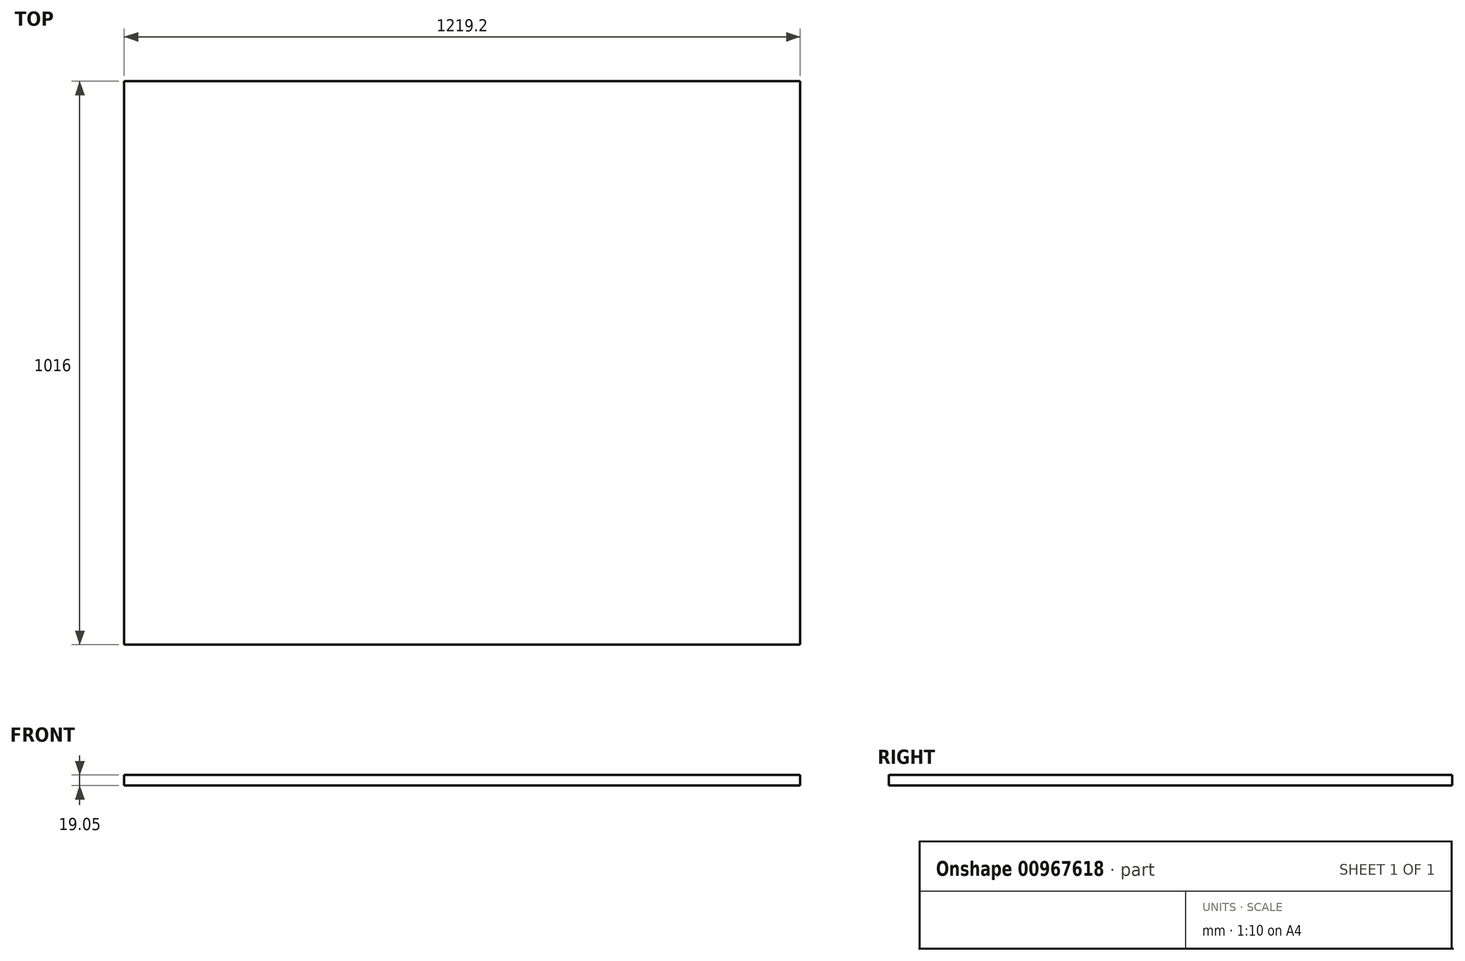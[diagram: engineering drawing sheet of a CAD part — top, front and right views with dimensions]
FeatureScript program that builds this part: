
annotation { "Feature Type Name" : "Feature", "Feature Type Description" : "" }
export const myFeature = defineFeature(function(context is Context, id is Id, definition is map)
    precondition{}
    {
        {
            var Q0;
            Q0=qCreatedBy(makeId("Top.planeOp"),FACE);
            var sketch = newSketch(context, id + "F0", { "sketchPlane" : qUnion([Q0])});
            skLineSegment(sketch, "E0.bottom", {"start": v(609.6, 508) * mm, "end": v(-609.6, 508) * mm});
            skLineSegment(sketch, "E0.top", {"start": v(609.6, -508) * mm, "end": v(-609.6, -508) * mm});
            skLineSegment(sketch, "E0.left", {"start": v(609.6, 508) * mm, "end": v(609.6, -508) * mm});
            skLineSegment(sketch, "E0.right", {"start": v(-609.6, 508) * mm, "end": v(-609.6, -508) * mm});
            skPoint(sketch, "E0.middle", {"position": v(0, 0) * mm});
            skSolve(sketch);
        }
        {
            var Q0;
            Q0 = qSketchRegion(id + "F0", true);
            extrude(context, id + "F1", {"entities" : qUnion([Q0]), "depth" : 19.05 * mm, "offsetDistance" : 25.4 * mm});
        }
    });
